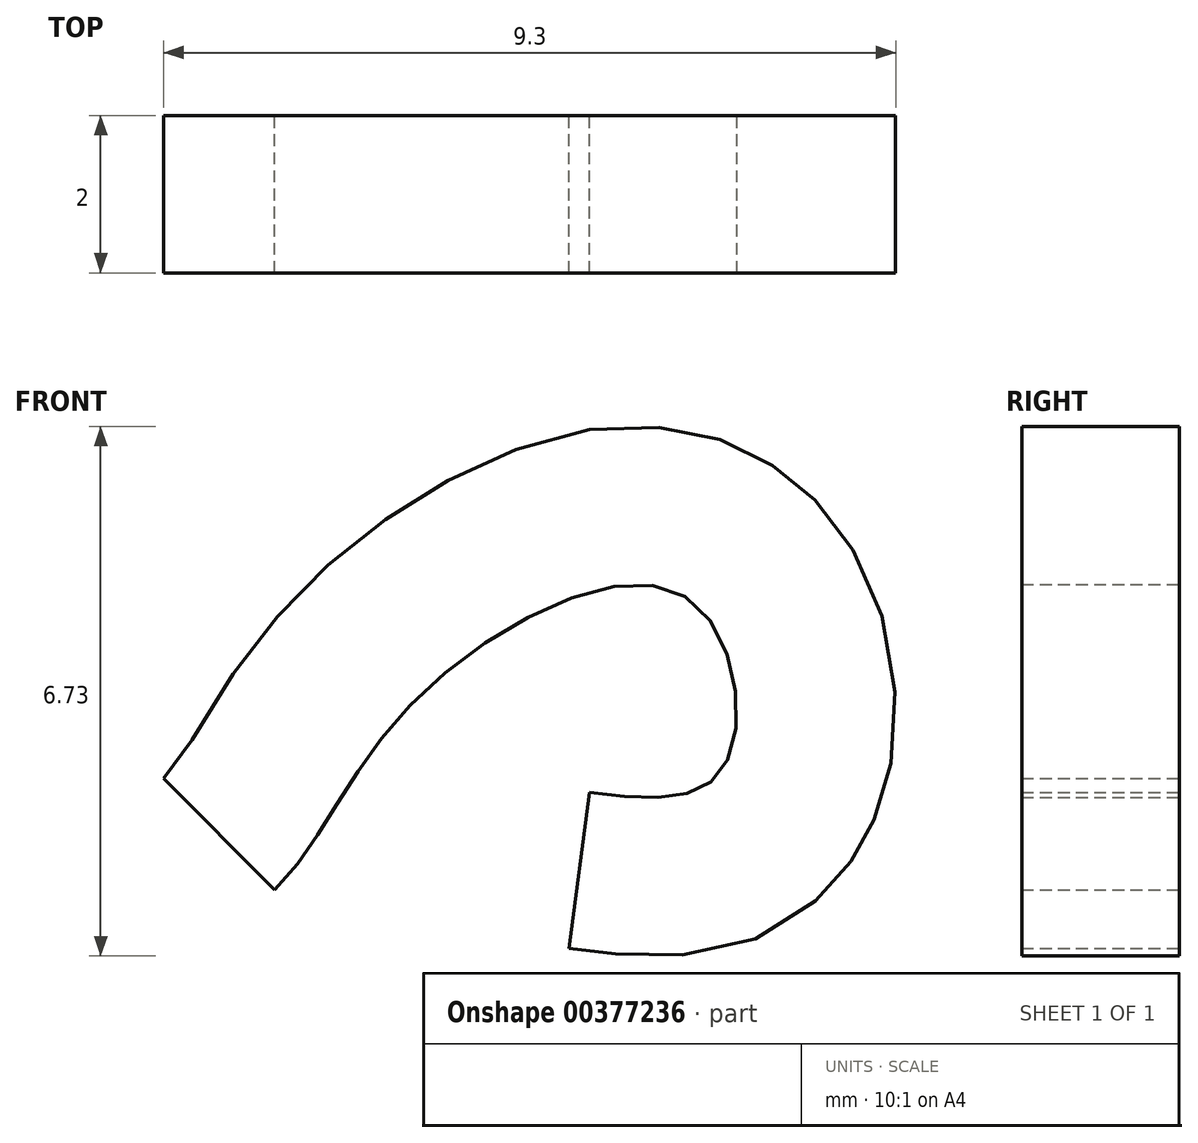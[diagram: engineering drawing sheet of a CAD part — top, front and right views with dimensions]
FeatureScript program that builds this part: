
annotation { "Feature Type Name" : "Feature", "Feature Type Description" : "" }
export const myFeature = defineFeature(function(context is Context, id is Id, definition is map)
    precondition{}
    {
        {
            var Q0;
            Q0=qCreatedBy(makeId("Front.planeOp"),FACE);
            var sketch = newSketch(context, id + "F0", { "sketchPlane" : qUnion([Q0])});
            skFitSpline(sketch, "E0", {"points": [v(0, 0) * mm, v(1.8, 2.42) * mm, v(5.21, 3.73) * mm, v(5.7, 1.55) * mm, v(4, 1.24) * mm], "startDerivative": vector(7.2, 7.2) * mm, "endDerivative": vector(-10.34, 1.36) * mm});
            skFitSpline(sketch, "E1.0", {"points": [v(-1.41, 1.41) * mm, v(-1.37, 1.46) * mm, v(-1.25, 1.6) * mm, v(-0.96, 2.06) * mm, v(-0.6, 2.64) * mm, v(-0.22, 3.17) * mm, v(0.13, 3.58) * mm, v(0.54, 4) * mm, v(1, 4.4) * mm, v(1.48, 4.76) * mm, v(2, 5.09) * mm, v(2.55, 5.38) * mm, v(3.13, 5.62) * mm, v(3.77, 5.8) * mm, v(4.36, 5.89) * mm, v(4.89, 5.88) * mm, v(5.3, 5.82) * mm, v(5.75, 5.7) * mm, v(6.11, 5.52) * mm, v(6.4, 5.35) * mm, v(6.65, 5.16) * mm, v(6.92, 4.9) * mm, v(7.18, 4.57) * mm, v(7.45, 4.13) * mm, v(7.68, 3.58) * mm, v(7.83, 2.93) * mm, v(7.89, 2.27) * mm, v(7.84, 1.71) * mm, v(7.73, 1.24) * mm, v(7.62, 0.92) * mm, v(7.5, 0.66) * mm, v(7.38, 0.46) * mm, v(7.25, 0.27) * mm, v(7.04, 0.02) * mm, v(6.75, -0.24) * mm, v(6.24, -0.56) * mm, v(5.63, -0.76) * mm, v(5.03, -0.83) * mm, v(4.52, -0.83) * mm, v(4.1, -0.79) * mm, v(3.85, -0.76) * mm, v(3.74, -0.74) * mm]});
            skLineSegment(sketch, "E2", {"start": v(-1.41, 1.41) * mm, "end": v(0, 0) * mm});
            skLineSegment(sketch, "E3", {"start": v(4, 1.24) * mm, "end": v(3.74, -0.74) * mm});
            skSolve(sketch);
        }
        {
            var Q0;
            Q0=makeQuery(id+"F0.imprint","IMPRINT",FACE,{"disambiguationData":[TD([[makeQuery(id+"F0.imprint","IMPRINT",EDGE,{"derivedFrom":sQuery(id+"F0.wireOp",EDGE,"E0")}),1.0]])]});
            extrude(context, id + "F1", {"entities" : qUnion([Q0]), "depth" : 2 * mm});
        }
    });
